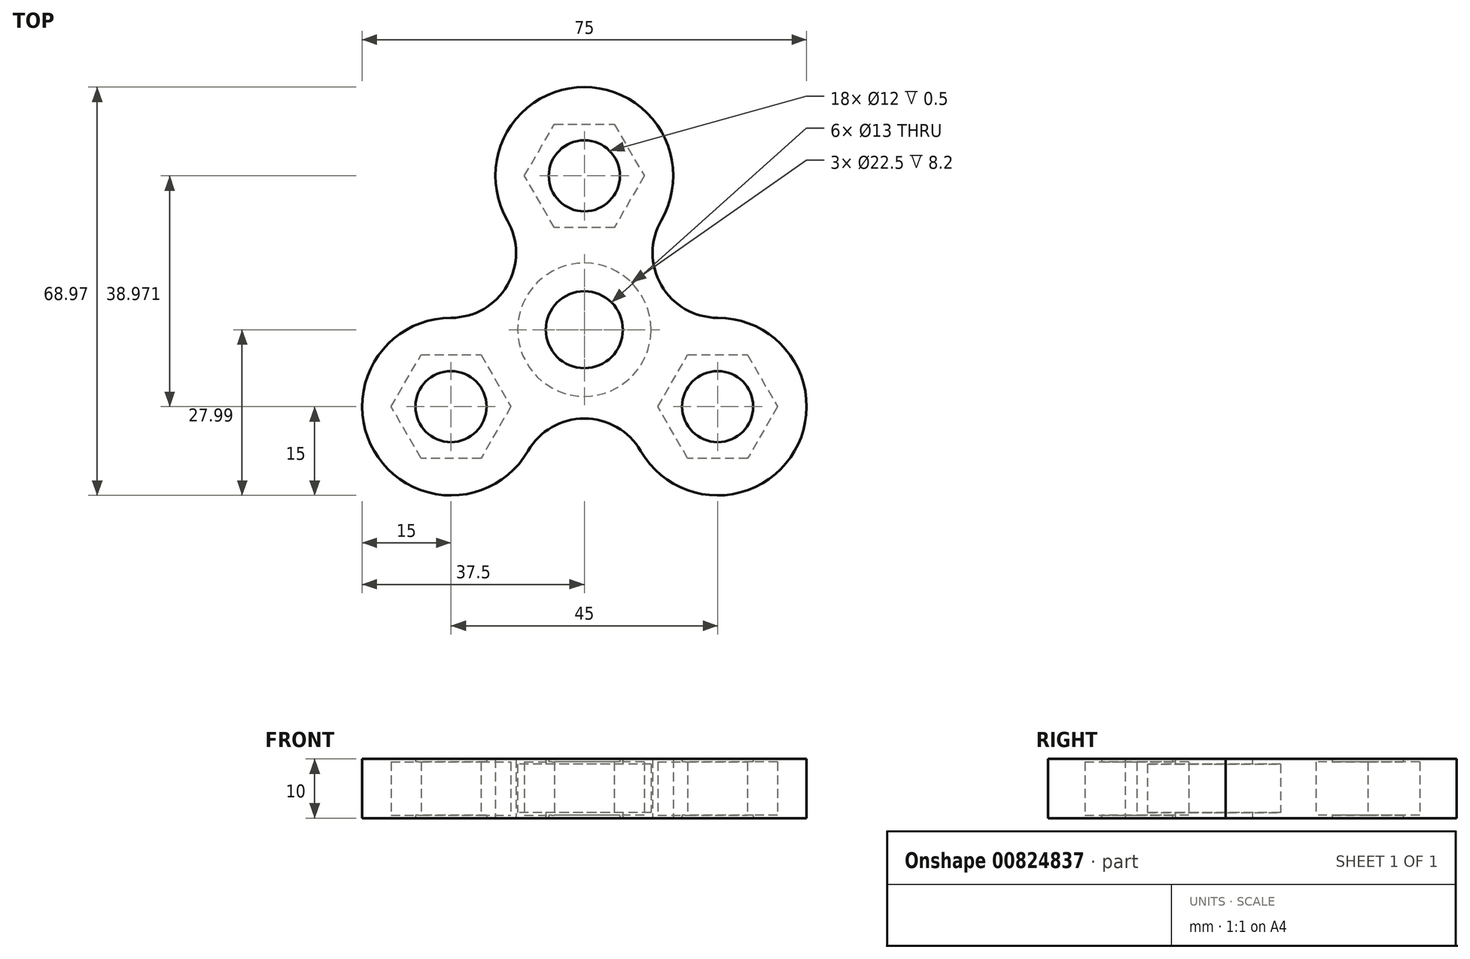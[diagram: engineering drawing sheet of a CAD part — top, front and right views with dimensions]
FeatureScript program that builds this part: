
annotation { "Feature Type Name" : "Feature", "Feature Type Description" : "" }
export const myFeature = defineFeature(function(context is Context, id is Id, definition is map)
    precondition{}
    {
        {
            var Q0;
            Q0=qCreatedBy(makeId("Top.planeOp"),FACE);
            var sketch = newSketch(context, id + "F0", { "sketchPlane" : qUnion([Q0])});
            skCircle(sketch, "E0.cCircle", {"center": v(0, 0) * mm, "radius": 13 * mm, "construction": true});
            skLineSegment(sketch, "E0.0", {"start": v(22.5, -13) * mm, "end": v(-22.5, -13) * mm, "construction": true});
            skLineSegment(sketch, "E0.1", {"start": v(-22.5, -13) * mm, "end": v(0, 25.98) * mm, "construction": true});
            skLineSegment(sketch, "E0.2", {"start": v(0, 25.98) * mm, "end": v(22.5, -13) * mm, "construction": true});
            skPoint(sketch, "E0.0.midPoint", {"position": v(0, -13) * mm});
            skLineSegment(sketch, "E1.0", {"start": v(0, -25.98) * mm, "end": v(-22.5, 13) * mm, "construction": true});
            skLineSegment(sketch, "E1.1", {"start": v(-22.5, 13) * mm, "end": v(22.5, 13) * mm, "construction": true});
            skLineSegment(sketch, "E1.2", {"start": v(22.5, 13) * mm, "end": v(0, -25.98) * mm, "construction": true});
            skPoint(sketch, "E1.0.midPoint", {"position": v(-11.25, -6.5) * mm});
            skCircle(sketch, "E2", {"center": v(0, 25.98) * mm, "radius": 15 * mm});
            skCircle(sketch, "E3", {"center": v(-22.5, -13) * mm, "radius": 15 * mm});
            skCircle(sketch, "E4", {"center": v(22.5, -13) * mm, "radius": 15 * mm});
            skArc(sketch, "E5", {"start": v(-22.5, 2) * mm, "mid": v(-13, 7.5) * mm, "end": v(-13, 18.48) * mm});
            skArc(sketch, "E6", {"start": v(13, 18.48) * mm, "mid": v(13, 7.5) * mm, "end": v(22.5, 2) * mm});
            skArc(sketch, "E7", {"start": v(9.5, -20.5) * mm, "mid": v(0, -15) * mm, "end": v(-9.5, -20.5) * mm});
            skCircle(sketch, "E8", {"center": v(0, 25.98) * mm, "radius": 6 * mm});
            skCircle(sketch, "E9", {"center": v(-22.5, -13) * mm, "radius": 6 * mm});
            skCircle(sketch, "E10", {"center": v(22.5, -13) * mm, "radius": 6 * mm});
            skCircle(sketch, "E11", {"center": v(0, 0) * mm, "radius": 6.5 * mm});
            skSolve(sketch);
        }
        {
            var Q0;
            Q0 = qSketchRegion(id + "F0", true);
            extrude(context, id + "F1", {"entities" : qUnion([Q0]), "endBound" : BoundingType.SYMMETRIC, "depth" : 10 * mm, "offsetDistance" : 25 * mm});
        }
        {
            var Q0;
            Q0=qCreatedBy(makeId("Top.planeOp"),FACE);
            var sketch = newSketch(context, id + "F2", { "sketchPlane" : qUnion([Q0])});
            skCircle(sketch, "E12", {"center": v(0, 0) * mm, "radius": 11.25 * mm});
            skSolve(sketch);
        }
        {
            var Q0;
            Q0 = qSketchRegion(id + "F2", true);
            extrude(context, id + "F3", {"entities" : qUnion([Q0]), "operationType" : NewBodyOperationType.REMOVE, "endBound" : BoundingType.SYMMETRIC, "depth" : 8.2 * mm, "offsetDistance" : 25 * mm});
        }
        {
            var Q0;
            Q0=qCreatedBy(makeId("Top.planeOp"),FACE);
            var sketch = newSketch(context, id + "F4", { "sketchPlane" : qUnion([Q0])});
            skLineSegment(sketch, "E13.0", {"start": v(22.5, -13) * mm, "end": v(-22.5, -13) * mm, "construction": true});
            skLineSegment(sketch, "E13.1", {"start": v(-22.5, -13) * mm, "end": v(0, 25.98) * mm, "construction": true});
            skLineSegment(sketch, "E13.2", {"start": v(0, 25.98) * mm, "end": v(22.5, -13) * mm, "construction": true});
            skCircle(sketch, "E14", {"center": v(0, 0) * mm, "radius": 6.5 * mm, "construction": true});
            skCircle(sketch, "E15.cCircle", {"center": v(22.5, -13) * mm, "radius": 8.75 * mm, "construction": true});
            skLineSegment(sketch, "E15.0", {"start": v(17.45, -4.24) * mm, "end": v(27.55, -4.24) * mm});
            skLineSegment(sketch, "E15.1", {"start": v(27.55, -4.24) * mm, "end": v(32.6, -13) * mm});
            skLineSegment(sketch, "E15.2", {"start": v(32.6, -13) * mm, "end": v(27.55, -21.74) * mm});
            skLineSegment(sketch, "E15.3", {"start": v(27.55, -21.74) * mm, "end": v(17.45, -21.74) * mm});
            skLineSegment(sketch, "E15.4", {"start": v(17.45, -21.74) * mm, "end": v(12.4, -13) * mm});
            skLineSegment(sketch, "E15.5", {"start": v(12.4, -13) * mm, "end": v(17.45, -4.24) * mm});
            skPoint(sketch, "E15.0.midPoint", {"position": v(22.5, -4.24) * mm});
            skCircle(sketch, "E16.cCircle", {"center": v(-22.5, -13) * mm, "radius": 8.75 * mm, "construction": true});
            skLineSegment(sketch, "E16.0", {"start": v(-17.45, -4.24) * mm, "end": v(-12.4, -13) * mm});
            skLineSegment(sketch, "E16.1", {"start": v(-12.4, -13) * mm, "end": v(-17.45, -21.74) * mm});
            skLineSegment(sketch, "E16.2", {"start": v(-17.45, -21.74) * mm, "end": v(-27.55, -21.74) * mm});
            skLineSegment(sketch, "E16.3", {"start": v(-27.55, -21.74) * mm, "end": v(-32.6, -13) * mm});
            skLineSegment(sketch, "E16.4", {"start": v(-32.6, -13) * mm, "end": v(-27.55, -4.24) * mm});
            skLineSegment(sketch, "E16.5", {"start": v(-27.55, -4.24) * mm, "end": v(-17.45, -4.24) * mm});
            skPoint(sketch, "E16.0.midPoint", {"position": v(-14.92, -8.62) * mm});
            skCircle(sketch, "E17.cCircle", {"center": v(0, 25.98) * mm, "radius": 8.75 * mm, "construction": true});
            skLineSegment(sketch, "E17.0", {"start": v(5.05, 17.23) * mm, "end": v(-5.05, 17.23) * mm});
            skLineSegment(sketch, "E17.1", {"start": v(-5.05, 17.23) * mm, "end": v(-10.1, 25.98) * mm});
            skLineSegment(sketch, "E17.2", {"start": v(-10.1, 25.98) * mm, "end": v(-5.05, 34.73) * mm});
            skLineSegment(sketch, "E17.3", {"start": v(-5.05, 34.73) * mm, "end": v(5.05, 34.73) * mm});
            skLineSegment(sketch, "E17.4", {"start": v(5.05, 34.73) * mm, "end": v(10.1, 25.98) * mm});
            skLineSegment(sketch, "E17.5", {"start": v(10.1, 25.98) * mm, "end": v(5.05, 17.23) * mm});
            skPoint(sketch, "E17.0.midPoint", {"position": v(0, 17.23) * mm});
            skSolve(sketch);
        }
        {
            var Q0;
            Q0 = qSketchRegion(id + "F4", true);
            extrude(context, id + "F5", {"entities" : qUnion([Q0]), "operationType" : NewBodyOperationType.REMOVE, "endBound" : BoundingType.SYMMETRIC, "depth" : 9 * mm, "offsetDistance" : 25 * mm});
        }
    });
